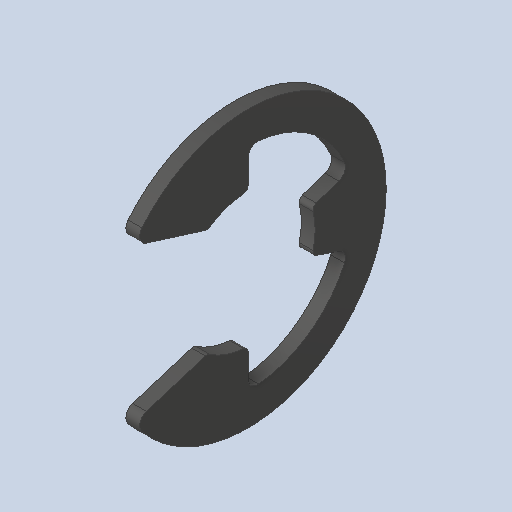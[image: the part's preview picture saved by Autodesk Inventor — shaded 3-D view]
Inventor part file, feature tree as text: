
AUTODESK INVENTOR PART (.ipt)
format: ipt  version: 2023.4 (Build 274418000, 418)  size: 113,664 bytes
history: native  units: in
note: dims shown in document units (in); Inventor stores cm internally (conversion verified against a paired STEP export)
features: fillet x1
ambient origin geometry x8: Origin, YZ Plane, XZ Plane, XY Plane, X Axis, Y Axis, Z Axis, Center Point
bodies: Solid1 (feature_tree)
feature tree (1):
  fillet  "Fillet2"  [1 undecoded]
note: 1 required parameter value undecoded (feature->parameter linkage not recoverable at this tier; creation-order binding heuristic only, values carry confidence <= 0.55)
